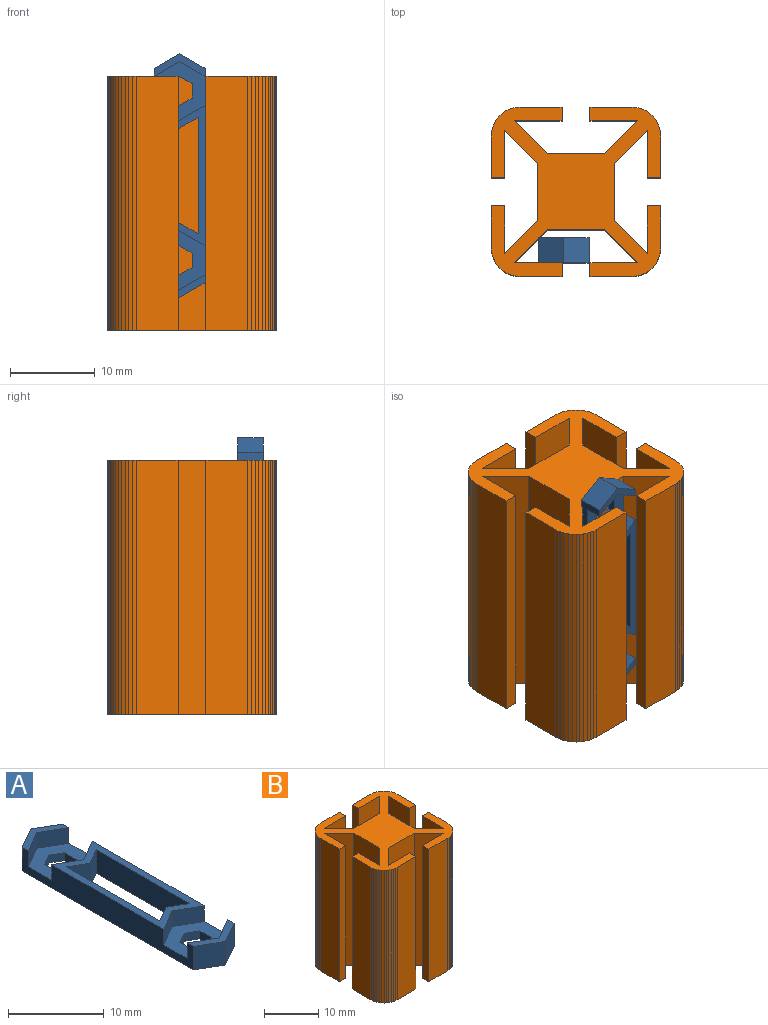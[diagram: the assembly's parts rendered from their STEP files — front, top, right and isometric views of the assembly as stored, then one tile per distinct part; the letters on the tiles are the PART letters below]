
ASSEMBLY  parts=2 mates=1
PART A: 38 faces, bbox 6x28.8x3 mm
  f0: plane 25.31x3mm, normal (1,0,0), area 62.1mm2, adj f8,f9,f10,f16,f17,f20,f21,f28
  f1: plane 25.31x3mm, normal (-1,0,0), area 62.1mm2, adj f8,f9,f11,f16,f18,f19,f21,f28
  f2: plane 1.7x1mm, normal (1,0,0), area 1.7mm2, adj f3,f7,f8,f9
  f3: plane 1.47x1mm, normal (0.5,-0.87,0), area 1.7mm2, adj f2,f4,f8,f9
  f4: plane 1.47x1mm, normal (-0.5,-0.87,0), area 1.7mm2, adj f3,f5,f8,f9
  f5: plane 1.7x1mm, normal (-1,0,0), area 1.7mm2, adj f4,f6,f8,f9
  f6: plane 1.47x1mm, normal (-0.5,0.87,0), area 1.7mm2, adj f5,f7,f8,f9
  f7: plane 1.47x1mm, normal (0.5,0.87,0), area 1.7mm2, adj f2,f6,f8,f9
  f8: plane 6.93x6mm, normal (0,0,1), area 23.7mm2, adj f0,f1,f2,f3,f4,f5,f6,f7
  f9: plane 28.78x6mm, normal (0,0,-1), area 92.3mm2, adj f0,f1,f2,f3,f4,f5,f6,f7
  f10: plane 3x2mm, normal (-0.5,-0.87,0), area 6.9mm2, adj f0,f8,f11,f16
  f11: plane 3x2mm, normal (0.5,-0.87,0), area 6.9mm2, adj f1,f8,f10,f16
  f12: plane 13.76x3mm, normal (-1,0,0), area 41.3mm2, adj f9,f13,f16,f31
  f13: plane 3x2.2mm, normal (0.5,0.87,0), area 7.6mm2, adj f9,f12,f14,f16
  f14: plane 3x2.2mm, normal (-0.5,0.87,0), area 7.6mm2, adj f9,f13,f15,f16
  f15: plane 13.76x3mm, normal (1,0,0), area 41.3mm2, adj f9,f14,f16,f32
  f16: plane 16.54x6mm, normal (0,0,1), area 33.8mm2, adj f0,f1,f10,f11,f12,f13,f14,f15
  f17: plane 3x2mm, normal (-0.5,0.87,0), area 6.9mm2, adj f0,f8,f18,f21
  f18: plane 3x2mm, normal (0.5,0.87,0), area 6.9mm2, adj f1,f8,f17,f21
  f19: plane 3x3mm, normal (-0.5,-0.87,0), area 10.4mm2, adj f1,f9,f20,f21
  f20: plane 3x3mm, normal (0.5,-0.87,0), area 10.4mm2, adj f0,f9,f19,f21
  f21: plane 6x2.66mm, normal (0,0,1), area 5.5mm2, adj f0,f1,f17,f18,f19,f20
  f22: plane 1.7x1mm, normal (1,0,0), area 1.7mm2, adj f9,f23,f27,f28
  f23: plane 1.47x1mm, normal (0.5,0.87,0), area 1.7mm2, adj f9,f22,f24,f28
  f24: plane 1.47x1mm, normal (-0.5,0.87,0), area 1.7mm2, adj f9,f23,f25,f28
  f25: plane 1.7x1mm, normal (-1,0,0), area 1.7mm2, adj f9,f24,f26,f28
  f26: plane 1.47x1mm, normal (-0.5,-0.87,0), area 1.7mm2, adj f9,f25,f27,f28
  f27: plane 1.47x1mm, normal (0.5,-0.87,0), area 1.7mm2, adj f9,f22,f26,f28
  f28: plane 6.93x6mm, normal (0,0,1), area 23.7mm2, adj f0,f1,f22,f23,f24,f25,f26,f27
  f29: plane 3x2mm, normal (-0.5,0.87,0), area 6.9mm2, adj f0,f16,f28,f30
  f30: plane 3x2mm, normal (0.5,0.87,0), area 6.9mm2, adj f1,f16,f28,f29
  f31: plane 3x2.2mm, normal (0.5,-0.87,0), area 7.6mm2, adj f9,f12,f16,f32
  f32: plane 3x2.2mm, normal (-0.5,-0.87,0), area 7.6mm2, adj f9,f15,f16,f31
  f33: plane 3x2mm, normal (-0.5,-0.87,0), area 6.9mm2, adj f0,f28,f34,f37
  f34: plane 3x2mm, normal (0.5,-0.87,0), area 6.9mm2, adj f1,f28,f33,f37
  f35: plane 3x3mm, normal (-0.5,0.87,0), area 10.4mm2, adj f1,f9,f36,f37
  f36: plane 3x3mm, normal (0.5,0.87,0), area 10.4mm2, adj f0,f9,f35,f37
  f37: plane 6x2.66mm, normal (0,0,1), area 5.5mm2, adj f0,f1,f33,f34,f35,f36
PART B: 86 faces, bbox 20x20x30 mm
  f0: plane 30x0.44mm, normal (0.98,0.2,0), area 13.4mm2, adj f1,f83,f84,f85
  f1: plane 30x0.42mm, normal (0.95,0.32,0), area 13.4mm2, adj f0,f2,f84,f85
  f2: plane 30x0.4mm, normal (0.9,0.44,0), area 13.4mm2, adj f1,f3,f84,f85
  f3: plane 30x0.37mm, normal (0.83,0.56,0), area 13.4mm2, adj f2,f4,f84,f85
  f4: plane 30x0.34mm, normal (0.75,0.66,0), area 13.4mm2, adj f3,f5,f84,f85
  f5: plane 30x0.34mm, normal (0.66,0.75,0), area 13.4mm2, adj f4,f6,f84,f85
  f6: plane 30x0.37mm, normal (0.56,0.83,0), area 13.4mm2, adj f5,f7,f84,f85
  f7: plane 30x0.4mm, normal (0.44,0.9,0), area 13.4mm2, adj f6,f8,f84,f85
  f8: plane 30x0.42mm, normal (0.32,0.95,0), area 13.4mm2, adj f7,f9,f84,f85
  f9: plane 30x0.44mm, normal (0.2,0.98,0), area 13.4mm2, adj f8,f10,f84,f85
  f10: plane 30x0.45mm, normal (0.07,1,0), area 13.4mm2, adj f9,f11,f84,f85
  f11: plane 30x4.94mm, normal (0,1,0), area 148.1mm2, adj f10,f12,f84,f85
  f12: plane 30x1.6mm, normal (-1,0,0), area 48mm2, adj f11,f13,f84,f85
  f13: plane 30x5.62mm, normal (0,-1,0), area 168.6mm2, adj f12,f14,f84,f85
  f14: plane 30x3.9mm, normal (-0.71,0.71,0), area 165.5mm2, adj f13,f15,f84,f85
  f15: plane 30x6.74mm, normal (0,1,0), area 202.1mm2, adj f14,f16,f84,f85
  f16: plane 30x3.9mm, normal (0.71,0.71,0), area 165.5mm2, adj f15,f17,f84,f85
  f17: plane 30x5.62mm, normal (0,-1,0), area 168.6mm2, adj f16,f18,f84,f85
  f18: plane 30x1.6mm, normal (1,0,0), area 48mm2, adj f17,f19,f84,f85
  f19: plane 30x4.94mm, normal (0,1,0), area 148.1mm2, adj f18,f20,f84,f85
  f20: plane 30x0.45mm, normal (-0.07,1,0), area 13.4mm2, adj f19,f21,f84,f85
  f21: plane 30x0.44mm, normal (-0.2,0.98,0), area 13.4mm2, adj f20,f22,f84,f85
  f22: plane 30x0.42mm, normal (-0.32,0.95,0), area 13.4mm2, adj f21,f23,f84,f85
  f23: plane 30x0.4mm, normal (-0.44,0.9,0), area 13.4mm2, adj f22,f24,f84,f85
  f24: plane 30x0.37mm, normal (-0.56,0.83,0), area 13.4mm2, adj f23,f25,f84,f85
  f25: plane 30x0.34mm, normal (-0.66,0.75,0), area 13.4mm2, adj f24,f26,f84,f85
  f26: plane 30x0.34mm, normal (-0.75,0.66,0), area 13.4mm2, adj f25,f27,f84,f85
  f27: plane 30x0.37mm, normal (-0.83,0.56,0), area 13.4mm2, adj f26,f28,f84,f85
  f28: plane 30x0.4mm, normal (-0.9,0.44,0), area 13.4mm2, adj f27,f29,f84,f85
  f29: plane 30x0.42mm, normal (-0.95,0.32,0), area 13.4mm2, adj f28,f30,f84,f85
  f30: plane 30x0.44mm, normal (-0.98,0.2,0), area 13.4mm2, adj f29,f31,f84,f85
  f31: plane 30x0.45mm, normal (-1,0.07,0), area 13.4mm2, adj f30,f32,f84,f85
  f32: plane 30x4.94mm, normal (-1,0,0), area 148.1mm2, adj f31,f33,f84,f85
  f33: plane 30x1.6mm, normal (0,-1,0), area 48mm2, adj f32,f34,f84,f85
  f34: plane 30x5.62mm, normal (1,0,0), area 168.6mm2, adj f33,f35,f84,f85
  f35: plane 30x3.9mm, normal (-0.71,-0.71,0), area 165.5mm2, adj f34,f36,f84,f85
  f36: plane 30x6.74mm, normal (-1,0,0), area 202.1mm2, adj f35,f37,f84,f85
  f37: plane 30x3.9mm, normal (-0.71,0.71,0), area 165.5mm2, adj f36,f38,f84,f85
  f38: plane 30x5.62mm, normal (1,0,0), area 168.6mm2, adj f37,f39,f84,f85
  f39: plane 30x1.6mm, normal (0,1,0), area 48mm2, adj f38,f40,f84,f85
  f40: plane 30x4.94mm, normal (-1,0,0), area 148.1mm2, adj f39,f41,f84,f85
  f41: plane 30x0.45mm, normal (-1,-0.07,0), area 13.4mm2, adj f40,f42,f84,f85
  f42: plane 30x0.44mm, normal (-0.98,-0.2,0), area 13.4mm2, adj f41,f43,f84,f85
  f43: plane 30x0.42mm, normal (-0.95,-0.32,0), area 13.4mm2, adj f42,f44,f84,f85
  f44: plane 30x0.4mm, normal (-0.9,-0.44,0), area 13.4mm2, adj f43,f45,f84,f85
  f45: plane 30x0.37mm, normal (-0.83,-0.56,0), area 13.4mm2, adj f44,f46,f84,f85
  f46: plane 30x0.34mm, normal (-0.75,-0.66,0), area 13.4mm2, adj f45,f47,f84,f85
  f47: plane 30x0.34mm, normal (-0.66,-0.75,0), area 13.4mm2, adj f46,f48,f84,f85
  f48: plane 30x0.37mm, normal (-0.56,-0.83,0), area 13.4mm2, adj f47,f49,f84,f85
  f49: plane 30x0.4mm, normal (-0.44,-0.9,0), area 13.4mm2, adj f48,f50,f84,f85
  f50: plane 30x0.42mm, normal (-0.32,-0.95,0), area 13.4mm2, adj f49,f51,f84,f85
  f51: plane 30x0.44mm, normal (-0.2,-0.98,0), area 13.4mm2, adj f50,f52,f84,f85
  f52: plane 30x0.45mm, normal (-0.07,-1,0), area 13.4mm2, adj f51,f53,f84,f85
  f53: plane 30x4.94mm, normal (0,-1,0), area 148.1mm2, adj f52,f54,f84,f85
  f54: plane 30x1.6mm, normal (1,0,0), area 48mm2, adj f53,f55,f84,f85
  f55: plane 30x5.62mm, normal (0,1,0), area 168.6mm2, adj f54,f56,f84,f85
  f56: plane 30x3.9mm, normal (0.71,-0.71,0), area 165.5mm2, adj f55,f57,f84,f85
  f57: plane 30x6.74mm, normal (0,-1,0), area 202.1mm2, adj f56,f58,f84,f85
  f58: plane 30x3.9mm, normal (-0.71,-0.71,0), area 165.5mm2, adj f57,f59,f84,f85
  f59: plane 30x5.62mm, normal (0,1,0), area 168.6mm2, adj f58,f60,f84,f85
  f60: plane 30x1.6mm, normal (-1,0,0), area 48mm2, adj f59,f61,f84,f85
  f61: plane 30x4.94mm, normal (0,-1,0), area 148.1mm2, adj f60,f62,f84,f85
  f62: plane 30x0.45mm, normal (0.07,-1,0), area 13.4mm2, adj f61,f63,f84,f85
  f63: plane 30x0.44mm, normal (0.2,-0.98,0), area 13.4mm2, adj f62,f64,f84,f85
  f64: plane 30x0.42mm, normal (0.32,-0.95,0), area 13.4mm2, adj f63,f65,f84,f85
  f65: plane 30x0.4mm, normal (0.44,-0.9,0), area 13.4mm2, adj f64,f66,f84,f85
  f66: plane 30x0.37mm, normal (0.56,-0.83,0), area 13.4mm2, adj f65,f67,f84,f85
  f67: plane 30x0.34mm, normal (0.66,-0.75,0), area 13.4mm2, adj f66,f68,f84,f85
  f68: plane 30x0.34mm, normal (0.75,-0.66,0), area 13.4mm2, adj f67,f69,f84,f85
  f69: plane 30x0.37mm, normal (0.83,-0.56,0), area 13.4mm2, adj f68,f70,f84,f85
  f70: plane 30x0.4mm, normal (0.9,-0.44,0), area 13.4mm2, adj f69,f71,f84,f85
  f71: plane 30x0.42mm, normal (0.95,-0.32,0), area 13.4mm2, adj f70,f72,f84,f85
  f72: plane 30x0.44mm, normal (0.98,-0.2,0), area 13.4mm2, adj f71,f73,f84,f85
  f73: plane 30x0.45mm, normal (1,-0.07,0), area 13.4mm2, adj f72,f74,f84,f85
  f74: plane 30x4.94mm, normal (1,0,0), area 148.1mm2, adj f73,f75,f84,f85
  f75: plane 30x1.6mm, normal (0,1,0), area 48mm2, adj f74,f76,f84,f85
  f76: plane 30x5.62mm, normal (-1,0,0), area 168.6mm2, adj f75,f77,f84,f85
  f77: plane 30x3.9mm, normal (0.71,0.71,0), area 165.5mm2, adj f76,f78,f84,f85
  f78: plane 30x6.74mm, normal (1,0,0), area 202.1mm2, adj f77,f79,f84,f85
  f79: plane 30x3.9mm, normal (0.71,-0.71,0), area 165.5mm2, adj f78,f80,f84,f85
  f80: plane 30x5.62mm, normal (-1,0,0), area 168.6mm2, adj f79,f81,f84,f85
  f81: plane 30x1.6mm, normal (0,-1,0), area 48mm2, adj f80,f82,f84,f85
  f82: plane 30x4.94mm, normal (1,0,0), area 148.1mm2, adj f81,f83,f84,f85
  f83: plane 30x0.45mm, normal (1,0.07,0), area 13.4mm2, adj f0,f82,f84,f85
  f84: plane 20x20mm, normal (0,0,1), area 202.8mm2, adj f0,f1,f2,f3,f4,f5,f6,f7
  f85: plane 20x20mm, normal (0,0,-1), area 202.8mm2, adj f0,f1,f2,f3,f4,f5,f6,f7
PLACE A rot(axis=(1,0,0),90deg) t=(-1.46,-5.4,18.27)mm
PLACE B at identity fixed
MATE slider A.f37 <-> B.f55  axis (0,-1,0) through (-4.46,-8.4,30)mm
